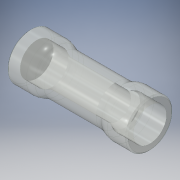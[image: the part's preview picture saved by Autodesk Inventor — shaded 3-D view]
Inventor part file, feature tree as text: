
AUTODESK INVENTOR PART (.ipt)
format: ipt  version: 2016 (Build 200138000, 138)  size: 181,760 bytes
history: native  units: in
note: dims shown in document units (in); Inventor stores cm internally (conversion verified against a paired STEP export)
features: plane x2, extrude x2, sketch x2, loft x1, mirror x1, shell x1, fillet x1, chamfer x1, other x1
ambient origin geometry x8: Origin, YZ Plane, XZ Plane, XY Plane, X Axis, Y Axis, Z Axis, Center Point
bodies: Solid1 (feature_tree)
feature tree (12):
  plane  "Work Plane1"
  extrude  "Extrusion1"  Depth=0.2in
  plane  "Work Plane2"
  sketch  "Sketch3"  dims[d3=0.225in d4=0.0in d5=0.15in d6=0.35in d7=0.0in d8=90.0deg d9=0.0in d10=90.0deg d11=0.175in d12=0.0in d13=0.05in d14=0.125in d15=0.01in d16=0.125in d17=45.0deg]
  loft  "Loft1"
  extrude  "Extrusion2"  Depth=0.125in
  mirror  "Mirror1"
  shell  "Shell1"  Thickness=0.0in
  fillet  "Fillet1"  [1 undecoded]
  chamfer  "Chamfer1"  Distance=0.175in
  sketch  "Sketch2"  dims[d1=0.2in d2=0.3in]
  other  "Edges1"
note: 1 required parameter value undecoded (feature->parameter linkage not recoverable at this tier; creation-order binding heuristic only, values carry confidence <= 0.55)
